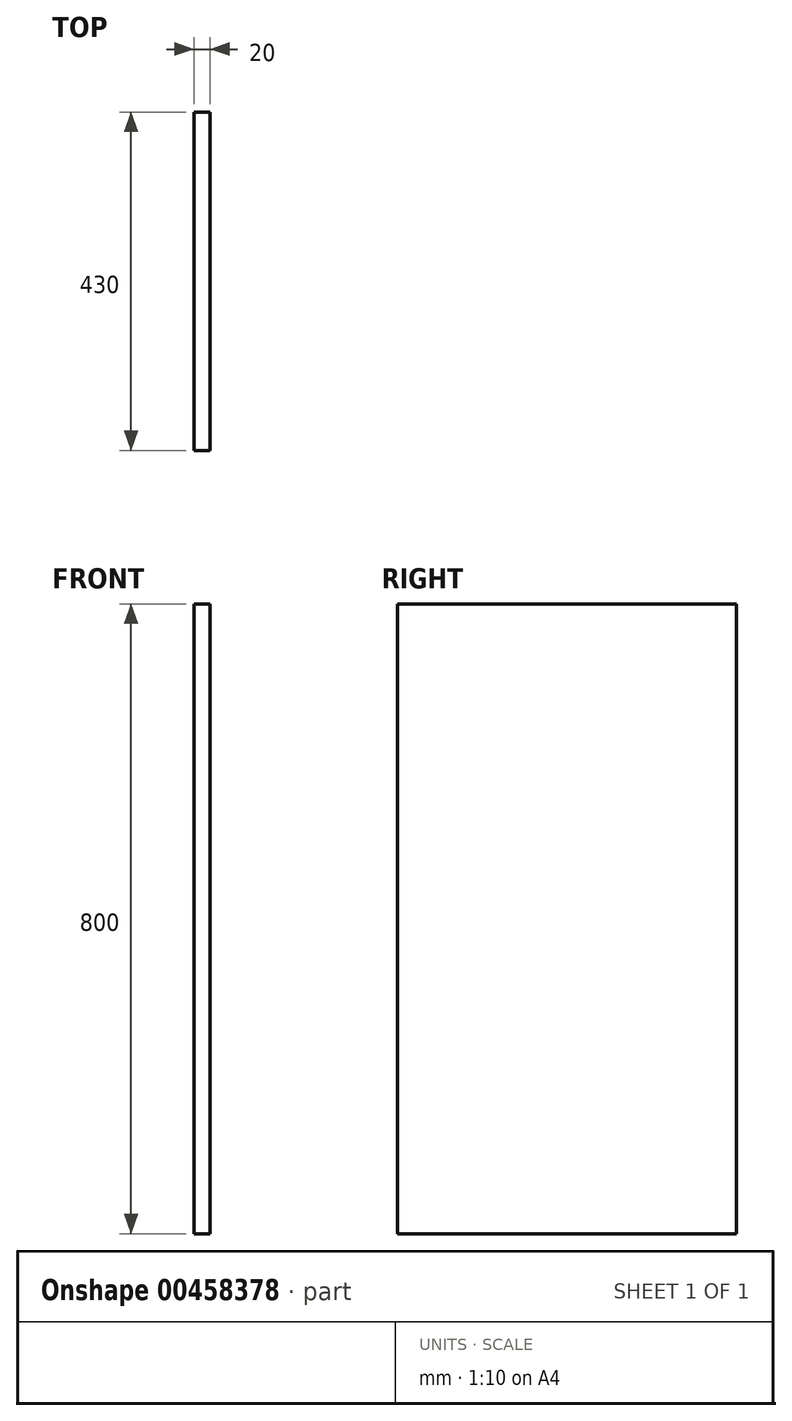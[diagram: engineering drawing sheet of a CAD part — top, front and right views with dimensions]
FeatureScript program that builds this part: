
annotation { "Feature Type Name" : "Feature", "Feature Type Description" : "" }
export const myFeature = defineFeature(function(context is Context, id is Id, definition is map)
    precondition{}
    {
        {
            var Q0;
            Q0=qCreatedBy(makeId("Right.planeOp"),FACE);
            var sketch = newSketch(context, id + "F0", { "sketchPlane" : qUnion([Q0])});
            skLineSegment(sketch, "E0.bottom", {"start": v(-414.91, 776.48) * mm, "end": v(15.09, 776.48) * mm});
            skLineSegment(sketch, "E0.top", {"start": v(-414.91, -23.52) * mm, "end": v(15.09, -23.52) * mm});
            skLineSegment(sketch, "E0.left", {"start": v(-414.91, 776.48) * mm, "end": v(-414.91, -23.52) * mm});
            skLineSegment(sketch, "E0.right", {"start": v(15.09, 776.48) * mm, "end": v(15.09, -23.52) * mm});
            skSolve(sketch);
        }
        {
            var Q0;
            Q0 = qSketchRegion(id + "F0", true);
            extrude(context, id + "F1", {"entities" : qUnion([Q0]), "depth" : 20 * mm});
        }
    });
